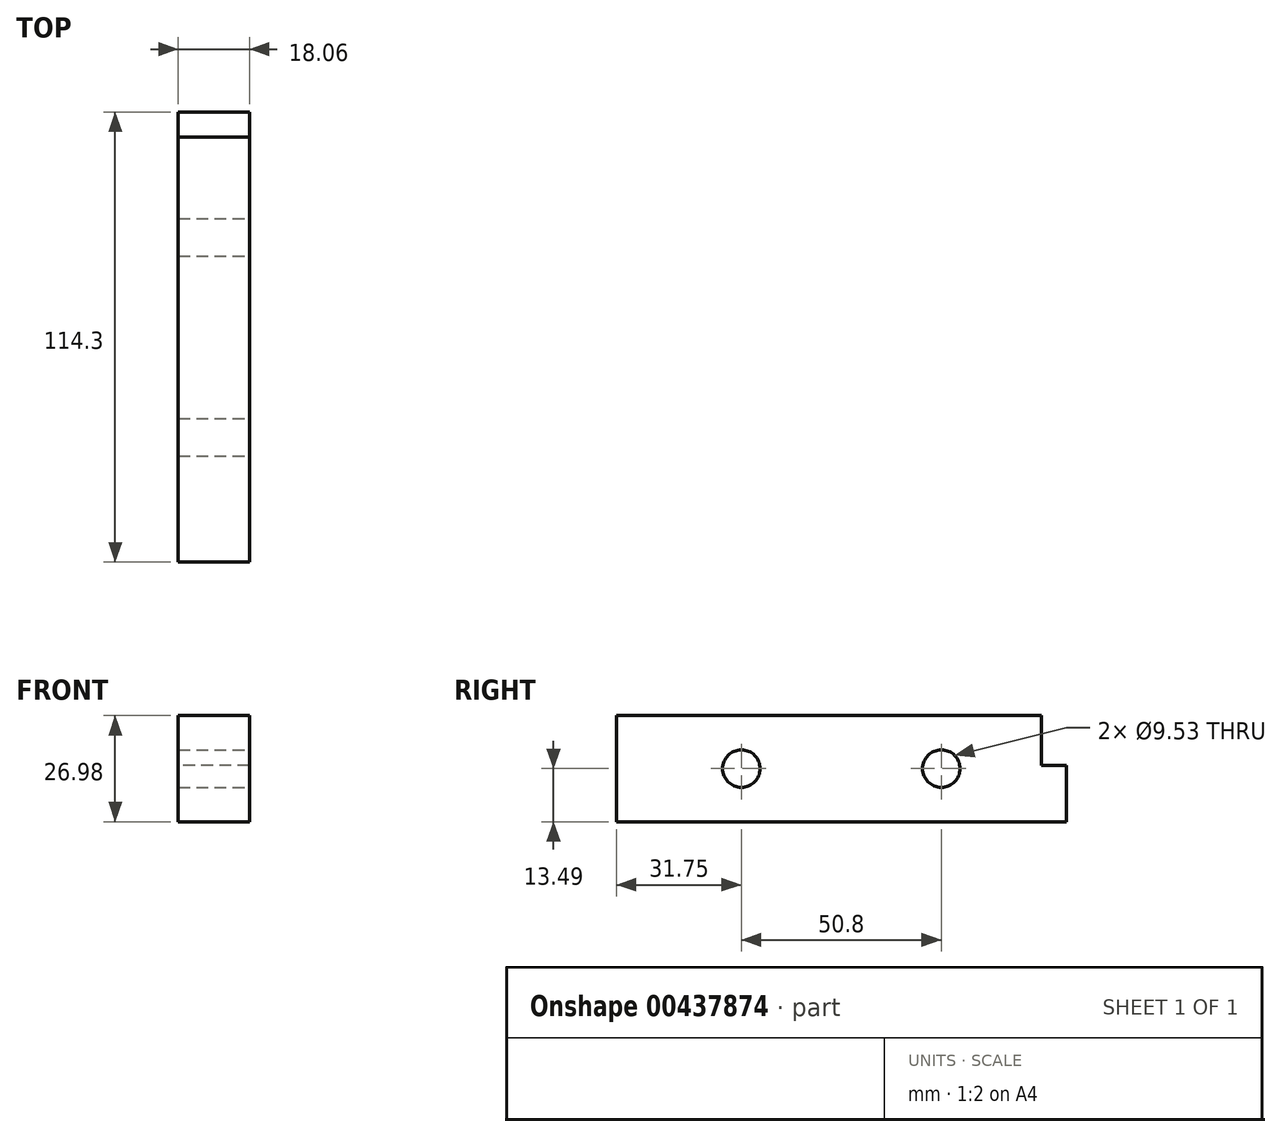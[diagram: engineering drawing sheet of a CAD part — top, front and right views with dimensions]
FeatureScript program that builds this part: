
annotation { "Feature Type Name" : "Feature", "Feature Type Description" : "" }
export const myFeature = defineFeature(function(context is Context, id is Id, definition is map)
    precondition{}
    {
        {
            var Q0;
            Q0=qCreatedBy(makeId("Right.planeOp"),FACE);
            var sketch = newSketch(context, id + "F0", { "sketchPlane" : qUnion([Q0])});
            skLineSegment(sketch, "E0.bottom", {"start": v(50.8, 13.5) * mm, "end": v(-57.15, 13.5) * mm});
            skLineSegment(sketch, "E0.top", {"start": v(57.15, -13.5) * mm, "end": v(-57.15, -13.5) * mm});
            skLineSegment(sketch, "E0.left", {"start": v(57.15, 0.8) * mm, "end": v(57.15, -13.5) * mm});
            skLineSegment(sketch, "E0.right", {"start": v(-57.15, 13.5) * mm, "end": v(-57.15, -13.5) * mm});
            skLineSegment(sketch, "E1.top", {"start": v(57.15, 0.8) * mm, "end": v(50.8, 0.8) * mm});
            skLineSegment(sketch, "E1.right", {"start": v(50.8, 13.5) * mm, "end": v(50.8, 0.8) * mm});
            skSolve(sketch);
        }
        {
            var Q0;
            Q0=makeQuery(id+"F0.imprint","IMPRINT",FACE,{"disambiguationData":[TD([[makeQuery(id+"F0.imprint","IMPRINT",EDGE,{"derivedFrom":sQuery(id+"F0.wireOp",EDGE,"E0.bottom")}),1.0]])]});
            extrude(context, id + "F1", {"entities" : qUnion([Q0]), "depth" : (18 + (1 / 16)) * mm, "symmetric" : true});
        }
        {
            var Q0;
            Q0=makeQuery(id+"F1.opExtrude","CAP_FACE",FACE,{"disambiguationData":[OSD([sQuery(id+"F0.wireOp",EDGE,"E0.bottom"),sQuery(id+"F0.wireOp",EDGE,"E0.top"),sQuery(id+"F0.wireOp",EDGE,"E0.left"),sQuery(id+"F0.wireOp",EDGE,"E0.right"),sQuery(id+"F0.wireOp",EDGE,"E1.top"),sQuery(id+"F0.wireOp",EDGE,"E1.right")])],"isStart":false});
            var sketch = newSketch(context, id + "F2", { "sketchPlane" : qUnion([Q0])});
            skPoint(sketch, "E2", {"position": v(-25.4, 0) * mm});
            skPoint(sketch, "E3", {"position": v(25.4, 0) * mm});
            skSolve(sketch);
        }
        {
            var Q0;
            Q0=sQuery(id+"F2.wireOp",VERTEX,"E2");
            var Q1;
            Q1=sQuery(id+"F2.wireOp",VERTEX,"E3");
            var Q2;
            Q2=makeQuery(id+"F1.opExtrude","SWEPT_BODY",BODY,{"disambiguationData":[OSD([sQuery(id+"F0.wireOp",EDGE,"E0.bottom"),sQuery(id+"F0.wireOp",EDGE,"E0.top"),sQuery(id+"F0.wireOp",EDGE,"E0.left"),sQuery(id+"F0.wireOp",EDGE,"E0.right"),sQuery(id+"F0.wireOp",EDGE,"E1.top"),sQuery(id+"F0.wireOp",EDGE,"E1.right")])]});
            hole(context, id + "F3", {"style" : HoleStyle.SIMPLE, "endStyle" : HoleEndStyle.BLIND, "holeDiameter" : 9.52 * mm, "holeDepth" : 25.4 * mm, "isTappedThrough" : true, "tappedDepth" : 12.7 * mm, "tapClearance" : 3, "locations" : qUnion([Q0, Q1]), "scope" : qUnion([Q2])});
        }
    });
